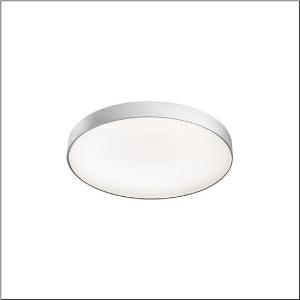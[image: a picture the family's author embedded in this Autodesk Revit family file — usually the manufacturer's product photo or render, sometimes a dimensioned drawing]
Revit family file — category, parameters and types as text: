
# Revit family: round_21_m_51mr36nd0421s
name_source: partatom
category: Lighting Fixtures
units: mm (PartAtom-declared; Revit-internal decimal feet)

## family parameters
Cut with Voids When Loaded = No
Host = Face
Light Source = No
Part Type = Normal
Room Calculation Point = No
Round Connector Dimension = Use Diameter
Shared = No

## types (1)
- Round 21 M (1 x LED, 7470 lm, 54.6 W, 4000K)
    Apparent Load = 55 VA
    CIE Flux Codes = 66 90 98 84 100
    Color Rendering = 80
    Color Temperature = 4000K
    Default Elevation = 1800 mm
    Description = Round 21 M, wall and ceiling luminaire, primary optical cover: micro prismatic cover, of PMMA, transparent, CAT 2 (L<= 3000cd/m²), light emission: direct/indirect distribution, primary light characteristic: symmetric, installation type: surface-mounted, suspended mounting, LED, rated luminous flux: 7.470lm, luminous efficacy: 137lm/W, light colour: 840, colour temperature: 4000K, control gear: DALI 2, with terminal, 5-pole, mains connection: 230V, AC, 50/60Hz, rated input power: 54.6W, housing, of aluminium, coated, silver, diameter: 600mm, height: 62mm, protection rating (complete): IP40, insulation class (complete): insulation class I (protective earthing), certification: CE, impact resistance: IK04, permissible operating ambient temperature: -10..+35°C, packaging unit: 1 piece
    Height = 87 mm
    Lamp = 1 x LED
    Lamp Light Flux = 7470 lm
    Lamp Power = 54.6 W
    Lamp count = 1
    Length = 600 mm
    Luminous efficacy = 137 lm/W
    Manufacturer = Siteco
    ModVariant = No
    Model = 51MR36ND0421S
    Mounting Place = Ceiling
    Mounting Type = Surface mounted
    Number of Poles = 1
    OnlyDefault = Yes
    Power Factor = 1
    Product Name = Round 21 M
    Product group = wall and ceiling luminaire
    ProductGroupID = 304
    Protection Class = Protection class I
    Protection Degree = IP 40
    RLX_Detail_Level = 1
    RLX_Emergency_Light_Flux = 0 lm
    RLX_Emergency_Type = 0
    RLX_Emergency_Type_DB = No
    RlxData = <blob elided: 19037 chars, md5=7d29d97a>
    Socket = socket
    Standby Power = 0 W
    System Light Flux = 7470 lm
    System Power = 55 W
    Type Comments = Product without accessories
    Type Image = l_1258301.jpg
    URL = http://relux.com
    VarID = ---
    Voltage = 0 V
    Weight = 0.00 kg
    Width = 0 mm  [stored 0 ft]

note: [stored X ft] marks values corroborated as IEEE doubles in the binary element streams (Revit-internal decimal feet)

## geometry (parser evidence)
native form markers: Blend x4, Sweep x11
no freeform markers — native parametric forms only
